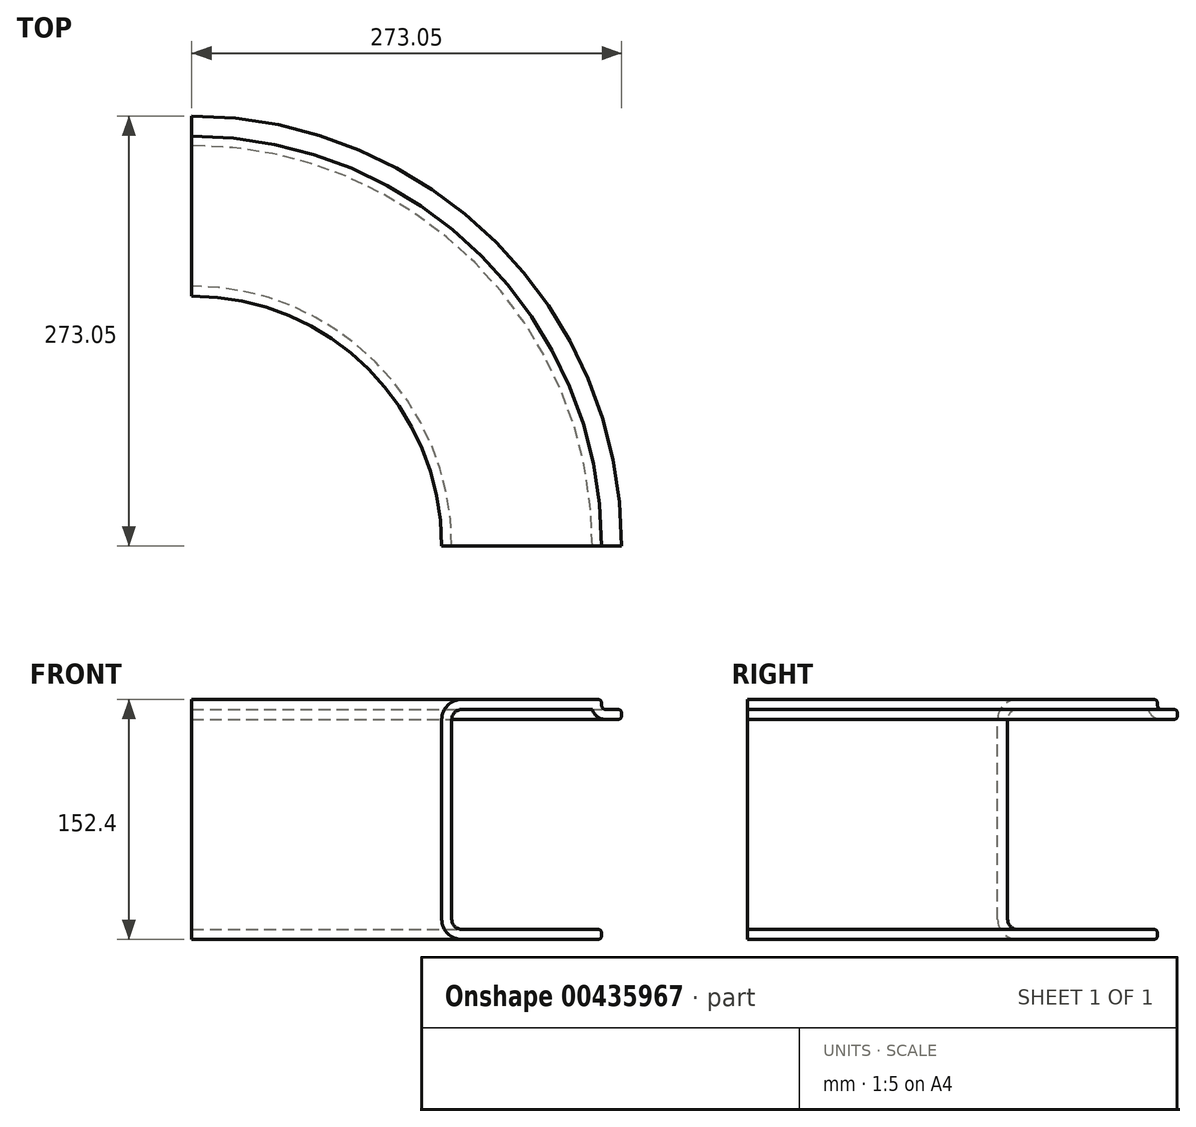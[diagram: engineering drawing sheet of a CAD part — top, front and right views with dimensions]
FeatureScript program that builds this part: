
annotation { "Feature Type Name" : "Feature", "Feature Type Description" : "" }
export const myFeature = defineFeature(function(context is Context, id is Id, definition is map)
    precondition{}
    {
        {
            var Q0;
            Q0=qCreatedBy(makeId("Front.planeOp"),FACE);
            var sketch = newSketch(context, id + "F0", { "sketchPlane" : qUnion([Q0])});
            skLineSegment(sketch, "E0", {"start": v(158.75, 12.7) * mm, "end": v(158.75, 139.7) * mm});
            skLineSegment(sketch, "E1", {"start": v(171.45, 152.4) * mm, "end": v(257.8, 152.4) * mm});
            skLineSegment(sketch, "E2", {"start": v(171.45, 0) * mm, "end": v(257.81, 0) * mm});
            skLineSegment(sketch, "E3", {"start": v(260.35, 149.86) * mm, "end": v(260.35, 148.6) * mm});
            skLineSegment(sketch, "E4", {"start": v(262.89, 146.05) * mm, "end": v(270.51, 146.05) * mm});
            skPoint(sketch, "E5.visualSharp", {"position": v(158.75, 152.4) * mm});
            skArc(sketch, "E5.filletArc", {"start": v(171.45, 152.4) * mm, "mid": v(162.47, 148.68) * mm, "end": v(158.75, 139.7) * mm});
            skPoint(sketch, "E6.visualSharp", {"position": v(158.75, 0) * mm});
            skArc(sketch, "E6.filletArc", {"start": v(158.75, 12.7) * mm, "mid": v(162.47, 3.72) * mm, "end": v(171.45, 0) * mm});
            skPoint(sketch, "E7.visualSharp", {"position": v(260.35, 152.4) * mm});
            skArc(sketch, "E7.filletArc", {"start": v(260.35, 149.86) * mm, "mid": v(259.6, 151.66) * mm, "end": v(257.8, 152.4) * mm});
            skPoint(sketch, "E8.visualSharp", {"position": v(260.35, 146.05) * mm});
            skArc(sketch, "E8.filletArc", {"start": v(260.35, 148.6) * mm, "mid": v(261.1, 146.8) * mm, "end": v(262.89, 146.05) * mm});
            skLineSegment(sketch, "E9.0", {"start": v(262.89, 139.7) * mm, "end": v(270.51, 139.7) * mm});
            skLineSegment(sketch, "E10.0", {"start": v(171.45, 146.05) * mm, "end": v(257.8, 146.05) * mm});
            skArc(sketch, "E11.0", {"start": v(254, 148.6) * mm, "mid": v(256.6, 142.3) * mm, "end": v(262.89, 139.7) * mm});
            skLineSegment(sketch, "E12.0", {"start": v(165.1, 12.7) * mm, "end": v(165.1, 139.7) * mm});
            skArc(sketch, "E13.0", {"start": v(171.45, 146.05) * mm, "mid": v(166.96, 144.2) * mm, "end": v(165.1, 139.7) * mm});
            skLineSegment(sketch, "E14.0", {"start": v(171.45, 6.35) * mm, "end": v(257.81, 6.35) * mm});
            skArc(sketch, "E15.0", {"start": v(165.1, 12.7) * mm, "mid": v(166.96, 8.2) * mm, "end": v(171.45, 6.35) * mm});
            skLineSegment(sketch, "E16", {"start": v(260.35, 2.54) * mm, "end": v(260.35, 3.8) * mm});
            skPoint(sketch, "E17.visualSharp", {"position": v(260.35, 6.35) * mm});
            skArc(sketch, "E17.filletArc", {"start": v(260.35, 3.8) * mm, "mid": v(259.6, 5.6) * mm, "end": v(257.81, 6.35) * mm});
            skPoint(sketch, "E18.visualSharp", {"position": v(260.35, 0) * mm});
            skArc(sketch, "E18.filletArc", {"start": v(257.81, 0) * mm, "mid": v(259.6, 0.74) * mm, "end": v(260.35, 2.54) * mm});
            skLineSegment(sketch, "E19", {"start": v(273.05, 143.51) * mm, "end": v(273.05, 142.24) * mm});
            skPoint(sketch, "E20.visualSharp", {"position": v(273.05, 146.05) * mm});
            skArc(sketch, "E20.filletArc", {"start": v(273.05, 143.51) * mm, "mid": v(272.3, 145.3) * mm, "end": v(270.51, 146.05) * mm});
            skPoint(sketch, "E21.visualSharp", {"position": v(273.05, 139.7) * mm});
            skArc(sketch, "E21.filletArc", {"start": v(270.51, 139.7) * mm, "mid": v(272.3, 140.44) * mm, "end": v(273.05, 142.24) * mm});
            skLineSegment(sketch, "E22", {"start": v(0, 0) * mm, "end": v(0, 136.8) * mm, "construction": true});
            skSolve(sketch);
        }
        {
            var Q0;
            Q0 = qSketchRegion(id + "F0", true);
            var Q1;
            Q1=sQuery(id+"F0.wireOp",EDGE,"E22");
            revolve(context, id + "F1", {"entities" : qUnion([Q0]), "axis" : qUnion([Q1]), "revolveType" : RevolveType.ONE_DIRECTION, "angle" : 90 * degree});
        }
    });
